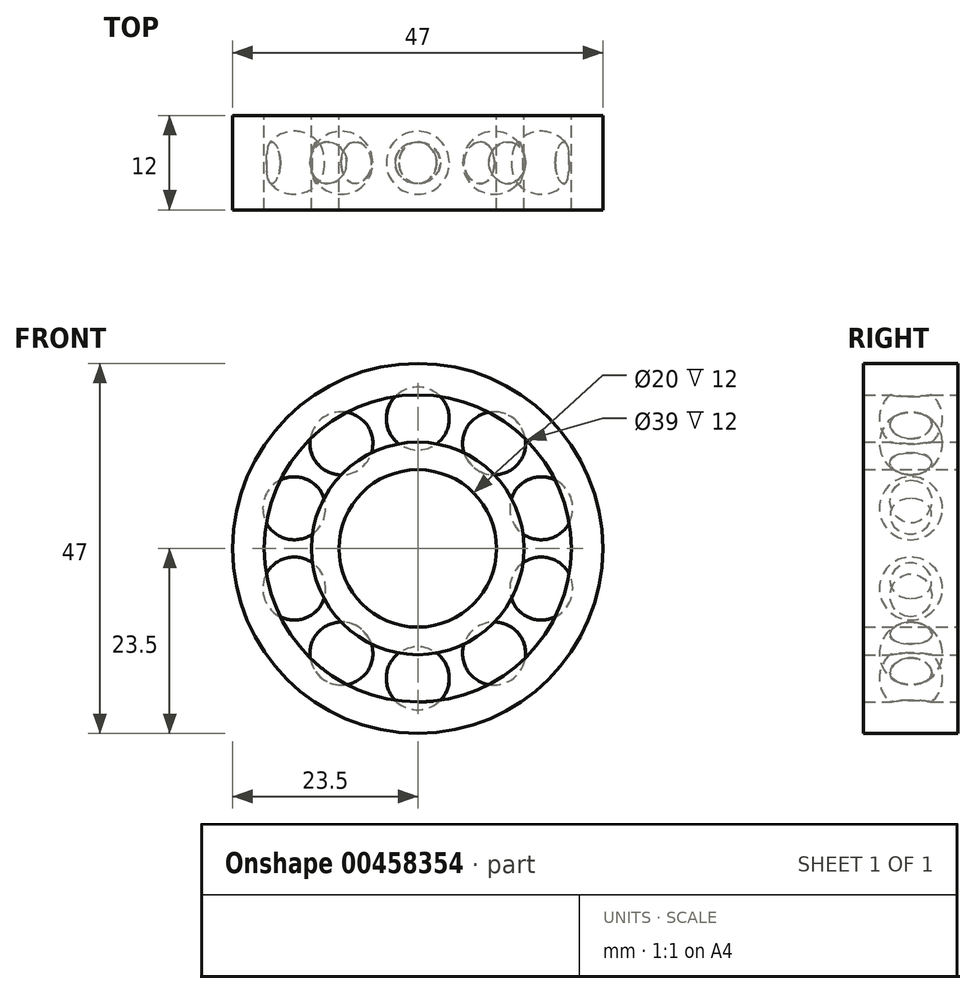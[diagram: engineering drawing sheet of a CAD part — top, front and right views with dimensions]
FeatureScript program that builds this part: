
annotation { "Feature Type Name" : "Feature", "Feature Type Description" : "" }
export const myFeature = defineFeature(function(context is Context, id is Id, definition is map)
    precondition{}
    {
        {
            var Q0;
            Q0=qCreatedBy(makeId("Front.planeOp"),FACE);
            var sketch = newSketch(context, id + "F0", { "sketchPlane" : qUnion([Q0])});
            skCircle(sketch, "E0", {"center": v(0, 0) * mm, "radius": 10 * mm});
            skCircle(sketch, "E1", {"center": v(0, 0) * mm, "radius": 13.5 * mm});
            skSolve(sketch);
        }
        {
            var Q0;
            Q0 = qSketchRegion(id + "F0", true);
            extrude(context, id + "F1", {"entities" : qUnion([Q0]), "depth" : 12 * mm});
        }
        {
            var Q0;
            Q0=qCreatedBy(makeId("Front.planeOp"),FACE);
            var sketch = newSketch(context, id + "F2", { "sketchPlane" : qUnion([Q0])});
            skCircle(sketch, "E2", {"center": v(0, 0) * mm, "radius": 19.5 * mm});
            skCircle(sketch, "E3", {"center": v(0, 0) * mm, "radius": 23.5 * mm});
            skSolve(sketch);
        }
        {
            var Q0;
            Q0=makeQuery(id+"F2.imprint","IMPRINT",FACE,{"disambiguationData":[TD([[makeQuery(id+"F2.imprint","IMPRINT",EDGE,{"derivedFrom":sQuery(id+"F2.wireOp",EDGE,"E2")}),-1.0]])]});
            extrude(context, id + "F3", {"entities" : qUnion([Q0]), "depth" : 12 * mm});
        }
        {
            var Q0;
            Q0=qCreatedBy(makeId("Front.planeOp"),FACE);
            cPlane(context, id + "F4", {"entities" : qUnion([Q0]), "cplaneType" : CPlaneType.OFFSET, "offset" : 6 * mm, "width" : 150 * mm, "height" : 150 * mm});
        }
        {
            var Q0;
            Q0=qCreatedBy(id+"F4.planeOp",FACE);
            var sketch = newSketch(context, id + "F5", { "sketchPlane" : qUnion([Q0])});
            skArc(sketch, "E4", {"start": v(0, 12.5) * mm, "mid": v(4, 16.5) * mm, "end": v(0, 20.5) * mm});
            skLineSegment(sketch, "E5", {"start": v(0, 20.5) * mm, "end": v(0, 12.5) * mm});
            skPoint(sketch, "E6.orphan", {"position": v(0, 24.96) * mm});
            skSolve(sketch);
        }
        {
            var Q0;
            Q0=makeQuery(id+"F5.imprint","IMPRINT",FACE,{"disambiguationData":[TD([[makeQuery(id+"F5.imprint","IMPRINT",EDGE,{"derivedFrom":sQuery(id+"F5.wireOp",EDGE,"E4")}),1.0]])]});
            var Q1;
            Q1=sQuery(id+"F5.wireOp",EDGE,"E5");
            revolve(context, id + "F6", {"entities" : qUnion([Q0]), "axis" : qUnion([Q1]), "revolveType" : RevolveType.FULL});
        }
        {
            var Q0;
            Q0=qCreatedBy(makeId("Right.planeOp"),FACE);
            var sketch = newSketch(context, id + "F7", { "sketchPlane" : qUnion([Q0])});
            skLineSegment(sketch, "E7", {"start": v(0, 0) * mm, "end": v(-152.1, 0) * mm, "construction": true});
            skSolve(sketch);
        }
        {
            var Q0;
            Q0=makeQuery(id+"F6.opRevolve","SWEPT_BODY",BODY,{"disambiguationData":[OSD([sQuery(id+"F5.wireOp",EDGE,"E4"),sQuery(id+"F5.wireOp",EDGE,"E5")])]});
            var Q1;
            Q1=sQuery(id+"F7.wireOp",EDGE,"E7");
            circularPattern(context, id + "F8", {"operationType" : NewBodyOperationType.ADD, "entities" : qUnion([Q0]), "axis" : qUnion([Q1]), "angle" : 360 * degree, "instanceCount" : 10, "equalSpace" : true});
        }
    });
